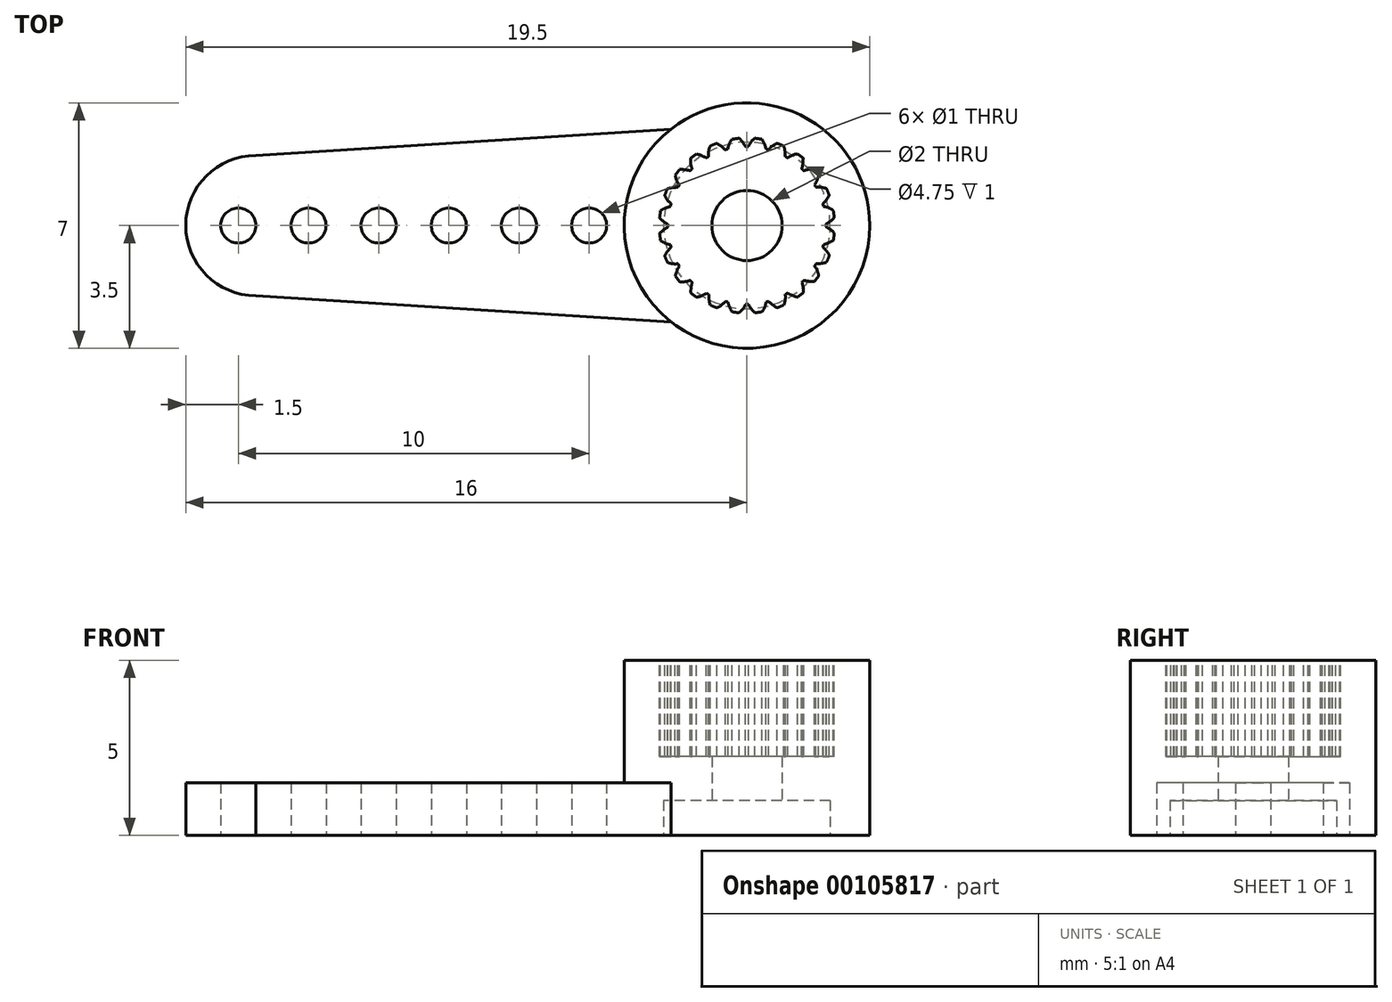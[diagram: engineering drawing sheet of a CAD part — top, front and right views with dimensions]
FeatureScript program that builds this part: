
annotation { "Feature Type Name" : "Feature", "Feature Type Description" : "" }
export const myFeature = defineFeature(function(context is Context, id is Id, definition is map)
    precondition{}
    {
        {
            var Q0;
            Q0=qCreatedBy(makeId("Top.planeOp"),FACE);
            var sketch = newSketch(context, id + "F0", { "sketchPlane" : qUnion([Q0])});
            skCircle(sketch, "E0", {"center": v(0, 0) * mm, "radius": 3.5 * mm});
            skCircle(sketch, "E1", {"center": v(-14, 0) * mm, "radius": 2 * mm});
            skLineSegment(sketch, "E2", {"start": v(-14, 2) * mm, "end": v(-2.17, 2.75) * mm});
            skLineSegment(sketch, "E3", {"start": v(-14, -2) * mm, "end": v(-2.17, -2.75) * mm});
            skCircle(sketch, "E4", {"center": v(0, 0) * mm, "radius": 1 * mm});
            skCircle(sketch, "E5", {"center": v(-14.5, 0) * mm, "radius": 0.5 * mm});
            skLineSegment(sketch, "E6", {"start": v(-16.68, 0) * mm, "end": v(5.78, 0) * mm, "construction": true});
            skCircle(sketch, "E7.1.0.0", {"center": v(-12.5, 0) * mm, "radius": 0.5 * mm});
            skCircle(sketch, "E7.2.0.0", {"center": v(-10.5, 0) * mm, "radius": 0.5 * mm});
            skLineSegment(sketch, "E7.direction1", {"start": v(-14.5, 0) * mm, "end": v(-12.5, 0) * mm, "construction": true});
            skCircle(sketch, "E8.0.3.0", {"center": v(-8.5, 0) * mm, "radius": 0.5 * mm});
            skCircle(sketch, "E8.0.4.0", {"center": v(-6.5, 0) * mm, "radius": 0.5 * mm});
            skCircle(sketch, "E8.0.5.0", {"center": v(-4.5, 0) * mm, "radius": 0.5 * mm});
            skLineSegment(sketch, "E9", {"start": v(0, 12.06) * mm, "end": v(0, -7.22) * mm, "construction": true});
            skSolve(sketch);
        }
        {
            var Q0;
            {var subQ6=sQuery(id+"F0.wireOp",EDGE,"E2");Q0=makeQuery(id+"F0.imprint","IMPRINT",FACE,{"disambiguationData":[TD([[makeQuery(id+"F0.imprint","IMPRINT",EDGE,{"derivedFrom":subQ6}),-1.0]])]});}
            var Q1;
            Q1=makeQuery(id+"F0.imprint","IMPRINT",FACE,{"disambiguationData":[TD([[makeQuery(id+"F0.imprint","IMPRINT",EDGE,{"derivedFrom":sQuery(id+"F0.wireOp",EDGE,"11ce5147-8903-4a82-81a3-89551e99495c")}),-1.0]])]});
            var Q2;
            Q2=makeQuery(id+"F0.imprint","IMPRINT",FACE,{"disambiguationData":[TD([[makeQuery(id+"F0.imprint","IMPRINT",EDGE,{"derivedFrom":sQuery(id+"F0.wireOp",EDGE,"E4")}),-1.0]])]});
            var Q3;
            Q3=makeQuery(id+"F0.imprint","IMPRINT",FACE,{"disambiguationData":[TD([[makeQuery(id+"F0.imprint","IMPRINT",EDGE,{"derivedFrom":sQuery(id+"F0.wireOp",EDGE,"E5")}),-1.0]])]});
            extrude(context, id + "F1", {"entities" : qUnion([Q0, Q1, Q2, Q3]), "depth" : 1.5 * mm});
        }
        {
            var Q0;
            Q0=makeQuery(id+"F0.imprint","IMPRINT",FACE,{"disambiguationData":[TD([[makeQuery(id+"F0.imprint","IMPRINT",EDGE,{"derivedFrom":sQuery(id+"F0.wireOp",EDGE,"E4")}),-1.0]])]});
            extrude(context, id + "F2", {"entities" : qUnion([Q0]), "operationType" : NewBodyOperationType.ADD, "depth" : 5 * mm});
        }
        {
            var Q0;
            Q0=makeQuery(id+"F0.imprint","IMPRINT",FACE,{"disambiguationData":[TD([[makeQuery(id+"F0.imprint","IMPRINT",EDGE,{"derivedFrom":sQuery(id+"F0.wireOp",EDGE,"E4")}),-1.0]])]});
            var sketch = newSketch(context, id + "F3", { "sketchPlane" : qUnion([Q0])});
            skCircle(sketch, "E10", {"center": v(0, 0) * mm, "radius": 2.37 * mm});
            skSolve(sketch);
        }
        {
            var Q0;
            Q0=qSketchRegion(id+"F3",true);
            extrude(context, id + "F4", {"entities" : qUnion([Q0]), "operationType" : NewBodyOperationType.REMOVE, "depth" : 1 * mm});
        }
        {
            var Q0;
            Q0=makeQuery(id+"F2.opExtrude","CAP_FACE",FACE,{"disambiguationData":[OSD([sQuery(id+"F0.wireOp",EDGE,"E0"),sQuery(id+"F0.wireOp",EDGE,"E4")])],"isStart":false});
            var sketch = newSketch(context, id + "F5", { "sketchPlane" : qUnion([Q0])});
            skCircle(sketch, "E11", {"center": v(0, 0) * mm, "radius": 2.25 * mm});
            skCircle(sketch, "E12", {"center": v(0, 0) * mm, "radius": 2.5 * mm, "construction": true});
            skLineSegment(sketch, "E13", {"start": v(0, 0) * mm, "end": v(0.98, 3.66) * mm, "construction": true});
            skLineSegment(sketch, "E14", {"start": v(0, 0) * mm, "end": v(2.5, 4.33) * mm, "construction": true});
            skArc(sketch, "E15", {"start": v(0.23, 2.49) * mm, "mid": v(0.12, 2.38) * mm, "end": v(0.04, 2.25) * mm});
            skArc(sketch, "E16", {"start": v(0.54, 2.18) * mm, "mid": v(0.5, 2.33) * mm, "end": v(0.43, 2.46) * mm});
            skArc(sketch, "E17", {"start": v(0.43, 2.46) * mm, "mid": v(0.33, 2.48) * mm, "end": v(0.23, 2.49) * mm});
            skCircle(sketch, "E18.2.0", {"center": v(0, 0) * mm, "radius": 2.25 * mm, "construction": true});
            skArc(sketch, "E19.1.1", {"start": v(-0.43, 2.46) * mm, "mid": v(-0.5, 2.33) * mm, "end": v(-0.54, 2.18) * mm});
            skArc(sketch, "E19.1.2", {"start": v(-0.23, 2.49) * mm, "mid": v(-0.33, 2.48) * mm, "end": v(-0.43, 2.46) * mm});
            skArc(sketch, "E19.1.3", {"start": v(-0.04, 2.25) * mm, "mid": v(-0.12, 2.38) * mm, "end": v(-0.23, 2.49) * mm});
            skArc(sketch, "E19.2.1", {"start": v(-1.05, 2.27) * mm, "mid": v(-1.1, 2.12) * mm, "end": v(-1.1, 1.97) * mm});
            skArc(sketch, "E19.2.2", {"start": v(-0.86, 2.35) * mm, "mid": v(-0.96, 2.3) * mm, "end": v(-1.05, 2.27) * mm});
            skArc(sketch, "E19.2.3", {"start": v(-0.62, 2.16) * mm, "mid": v(-0.73, 2.26) * mm, "end": v(-0.86, 2.35) * mm});
            skArc(sketch, "E20.2.3.0", {"start": v(-1.6, 1.92) * mm, "mid": v(-1.6, 1.77) * mm, "end": v(-1.56, 1.62) * mm});
            skArc(sketch, "E20.6.3.0", {"start": v(-1.44, 2.04) * mm, "mid": v(-1.52, 1.98) * mm, "end": v(-1.6, 1.92) * mm});
            skArc(sketch, "E20.10.3.0", {"start": v(-1.16, 1.93) * mm, "mid": v(-1.3, 2) * mm, "end": v(-1.44, 2.04) * mm});
            skArc(sketch, "E20.2.4.0", {"start": v(-2.04, 1.44) * mm, "mid": v(-2, 1.3) * mm, "end": v(-1.93, 1.16) * mm});
            skArc(sketch, "E20.6.4.0", {"start": v(-1.92, 1.6) * mm, "mid": v(-1.98, 1.52) * mm, "end": v(-2.04, 1.44) * mm});
            skArc(sketch, "E20.10.4.0", {"start": v(-1.62, 1.56) * mm, "mid": v(-1.77, 1.6) * mm, "end": v(-1.92, 1.6) * mm});
            skArc(sketch, "E20.2.5.0", {"start": v(-2.35, 0.86) * mm, "mid": v(-2.27, 0.73) * mm, "end": v(-2.16, 0.62) * mm});
            skArc(sketch, "E20.6.5.0", {"start": v(-2.27, 1.05) * mm, "mid": v(-2.3, 0.96) * mm, "end": v(-2.35, 0.86) * mm});
            skArc(sketch, "E20.10.5.0", {"start": v(-1.97, 1.1) * mm, "mid": v(-2.12, 1.08) * mm, "end": v(-2.27, 1.05) * mm});
            skArc(sketch, "E20.2.6.0", {"start": v(-2.49, 0.23) * mm, "mid": v(-2.38, 0.12) * mm, "end": v(-2.25, 0.04) * mm});
            skArc(sketch, "E20.6.6.0", {"start": v(-2.46, 0.43) * mm, "mid": v(-2.48, 0.33) * mm, "end": v(-2.49, 0.23) * mm});
            skArc(sketch, "E20.10.6.0", {"start": v(-2.18, 0.54) * mm, "mid": v(-2.33, 0.5) * mm, "end": v(-2.46, 0.43) * mm});
            skArc(sketch, "E20.2.7.0", {"start": v(-2.46, -0.43) * mm, "mid": v(-2.33, -0.5) * mm, "end": v(-2.18, -0.54) * mm});
            skArc(sketch, "E20.6.7.0", {"start": v(-2.49, -0.22) * mm, "mid": v(-2.48, -0.33) * mm, "end": v(-2.46, -0.43) * mm});
            skArc(sketch, "E20.10.7.0", {"start": v(-2.25, -0.04) * mm, "mid": v(-2.38, -0.12) * mm, "end": v(-2.49, -0.22) * mm});
            skArc(sketch, "E20.2.8.0", {"start": v(-2.27, -1.05) * mm, "mid": v(-2.12, -1.1) * mm, "end": v(-1.97, -1.1) * mm});
            skArc(sketch, "E20.6.8.0", {"start": v(-2.35, -0.86) * mm, "mid": v(-2.3, -0.96) * mm, "end": v(-2.27, -1.05) * mm});
            skArc(sketch, "E20.10.8.0", {"start": v(-2.16, -0.62) * mm, "mid": v(-2.26, -0.73) * mm, "end": v(-2.35, -0.86) * mm});
            skArc(sketch, "E20.2.9.0", {"start": v(-1.92, -1.6) * mm, "mid": v(-1.77, -1.6) * mm, "end": v(-1.62, -1.56) * mm});
            skArc(sketch, "E20.6.9.0", {"start": v(-2.04, -1.44) * mm, "mid": v(-1.98, -1.52) * mm, "end": v(-1.92, -1.6) * mm});
            skArc(sketch, "E20.10.9.0", {"start": v(-1.93, -1.16) * mm, "mid": v(-2, -1.3) * mm, "end": v(-2.04, -1.44) * mm});
            skArc(sketch, "E20.2.10.0", {"start": v(-1.44, -2.04) * mm, "mid": v(-1.3, -2) * mm, "end": v(-1.16, -1.93) * mm});
            skArc(sketch, "E20.6.10.0", {"start": v(-1.6, -1.92) * mm, "mid": v(-1.52, -1.98) * mm, "end": v(-1.44, -2.04) * mm});
            skArc(sketch, "E20.10.10.0", {"start": v(-1.56, -1.62) * mm, "mid": v(-1.6, -1.77) * mm, "end": v(-1.6, -1.92) * mm});
            skArc(sketch, "E20.2.11.0", {"start": v(-0.86, -2.35) * mm, "mid": v(-0.73, -2.27) * mm, "end": v(-0.62, -2.16) * mm});
            skArc(sketch, "E20.6.11.0", {"start": v(-1.05, -2.27) * mm, "mid": v(-0.96, -2.3) * mm, "end": v(-0.86, -2.35) * mm});
            skArc(sketch, "E20.10.11.0", {"start": v(-1.1, -1.97) * mm, "mid": v(-1.08, -2.12) * mm, "end": v(-1.05, -2.27) * mm});
            skArc(sketch, "E20.2.12.0", {"start": v(-0.23, -2.49) * mm, "mid": v(-0.12, -2.38) * mm, "end": v(-0.04, -2.25) * mm});
            skArc(sketch, "E20.6.12.0", {"start": v(-0.43, -2.46) * mm, "mid": v(-0.33, -2.48) * mm, "end": v(-0.23, -2.49) * mm});
            skArc(sketch, "E20.10.12.0", {"start": v(-0.54, -2.18) * mm, "mid": v(-0.5, -2.33) * mm, "end": v(-0.43, -2.46) * mm});
            skArc(sketch, "E20.2.13.0", {"start": v(0.43, -2.46) * mm, "mid": v(0.5, -2.33) * mm, "end": v(0.54, -2.18) * mm});
            skArc(sketch, "E20.6.13.0", {"start": v(0.22, -2.49) * mm, "mid": v(0.33, -2.48) * mm, "end": v(0.43, -2.46) * mm});
            skArc(sketch, "E20.10.13.0", {"start": v(0.04, -2.25) * mm, "mid": v(0.12, -2.38) * mm, "end": v(0.23, -2.49) * mm});
            skArc(sketch, "E20.2.14.0", {"start": v(1.05, -2.27) * mm, "mid": v(1.1, -2.12) * mm, "end": v(1.1, -1.97) * mm});
            skArc(sketch, "E20.6.14.0", {"start": v(0.86, -2.35) * mm, "mid": v(0.96, -2.3) * mm, "end": v(1.05, -2.27) * mm});
            skArc(sketch, "E20.10.14.0", {"start": v(0.62, -2.16) * mm, "mid": v(0.73, -2.26) * mm, "end": v(0.86, -2.35) * mm});
            skArc(sketch, "E20.2.15.0", {"start": v(1.6, -1.92) * mm, "mid": v(1.6, -1.77) * mm, "end": v(1.56, -1.62) * mm});
            skArc(sketch, "E20.6.15.0", {"start": v(1.44, -2.04) * mm, "mid": v(1.52, -1.98) * mm, "end": v(1.6, -1.92) * mm});
            skArc(sketch, "E20.10.15.0", {"start": v(1.16, -1.93) * mm, "mid": v(1.3, -2) * mm, "end": v(1.44, -2.04) * mm});
            skArc(sketch, "E20.2.16.0", {"start": v(2.04, -1.44) * mm, "mid": v(2, -1.3) * mm, "end": v(1.93, -1.16) * mm});
            skArc(sketch, "E20.6.16.0", {"start": v(1.92, -1.6) * mm, "mid": v(1.98, -1.52) * mm, "end": v(2.04, -1.44) * mm});
            skArc(sketch, "E20.10.16.0", {"start": v(1.62, -1.56) * mm, "mid": v(1.77, -1.6) * mm, "end": v(1.92, -1.6) * mm});
            skArc(sketch, "E20.2.17.0", {"start": v(2.35, -0.86) * mm, "mid": v(2.27, -0.73) * mm, "end": v(2.16, -0.62) * mm});
            skArc(sketch, "E20.6.17.0", {"start": v(2.27, -1.05) * mm, "mid": v(2.3, -0.96) * mm, "end": v(2.35, -0.86) * mm});
            skArc(sketch, "E20.10.17.0", {"start": v(1.97, -1.1) * mm, "mid": v(2.12, -1.08) * mm, "end": v(2.27, -1.05) * mm});
            skArc(sketch, "E20.2.18.0", {"start": v(2.49, -0.23) * mm, "mid": v(2.38, -0.12) * mm, "end": v(2.25, -0.04) * mm});
            skArc(sketch, "E20.6.18.0", {"start": v(2.46, -0.43) * mm, "mid": v(2.48, -0.33) * mm, "end": v(2.49, -0.23) * mm});
            skArc(sketch, "E20.10.18.0", {"start": v(2.18, -0.54) * mm, "mid": v(2.33, -0.5) * mm, "end": v(2.46, -0.43) * mm});
            skArc(sketch, "E20.2.19.0", {"start": v(2.46, 0.43) * mm, "mid": v(2.33, 0.5) * mm, "end": v(2.18, 0.54) * mm});
            skArc(sketch, "E20.6.19.0", {"start": v(2.49, 0.22) * mm, "mid": v(2.48, 0.33) * mm, "end": v(2.46, 0.43) * mm});
            skArc(sketch, "E20.10.19.0", {"start": v(2.25, 0.04) * mm, "mid": v(2.38, 0.12) * mm, "end": v(2.49, 0.22) * mm});
            skArc(sketch, "E20.2.20.0", {"start": v(2.27, 1.05) * mm, "mid": v(2.12, 1.1) * mm, "end": v(1.97, 1.1) * mm});
            skArc(sketch, "E20.6.20.0", {"start": v(2.35, 0.86) * mm, "mid": v(2.3, 0.96) * mm, "end": v(2.27, 1.05) * mm});
            skArc(sketch, "E20.10.20.0", {"start": v(2.16, 0.62) * mm, "mid": v(2.26, 0.73) * mm, "end": v(2.35, 0.86) * mm});
            skArc(sketch, "E20.2.21.0", {"start": v(1.92, 1.6) * mm, "mid": v(1.77, 1.6) * mm, "end": v(1.62, 1.56) * mm});
            skArc(sketch, "E20.6.21.0", {"start": v(2.04, 1.44) * mm, "mid": v(1.98, 1.52) * mm, "end": v(1.92, 1.6) * mm});
            skArc(sketch, "E20.10.21.0", {"start": v(1.93, 1.16) * mm, "mid": v(2, 1.3) * mm, "end": v(2.04, 1.44) * mm});
            skArc(sketch, "E20.2.22.0", {"start": v(1.44, 2.04) * mm, "mid": v(1.3, 2) * mm, "end": v(1.16, 1.93) * mm});
            skArc(sketch, "E20.6.22.0", {"start": v(1.6, 1.92) * mm, "mid": v(1.52, 1.98) * mm, "end": v(1.44, 2.04) * mm});
            skArc(sketch, "E20.10.22.0", {"start": v(1.56, 1.62) * mm, "mid": v(1.6, 1.77) * mm, "end": v(1.6, 1.92) * mm});
            skArc(sketch, "E20.2.23.0", {"start": v(0.86, 2.35) * mm, "mid": v(0.73, 2.27) * mm, "end": v(0.62, 2.16) * mm});
            skArc(sketch, "E20.6.23.0", {"start": v(1.05, 2.27) * mm, "mid": v(0.96, 2.3) * mm, "end": v(0.86, 2.35) * mm});
            skArc(sketch, "E20.10.23.0", {"start": v(1.1, 1.97) * mm, "mid": v(1.08, 2.12) * mm, "end": v(1.05, 2.27) * mm});
            skSolve(sketch);
        }
        {
            var Q0;
            Q0=qSketchRegion(id+"F5",true);
            extrude(context, id + "F6", {"entities" : qUnion([Q0]), "operationType" : NewBodyOperationType.REMOVE, "oppositeDirection" : true, "depth" : 2.75 * mm});
        }
    });
